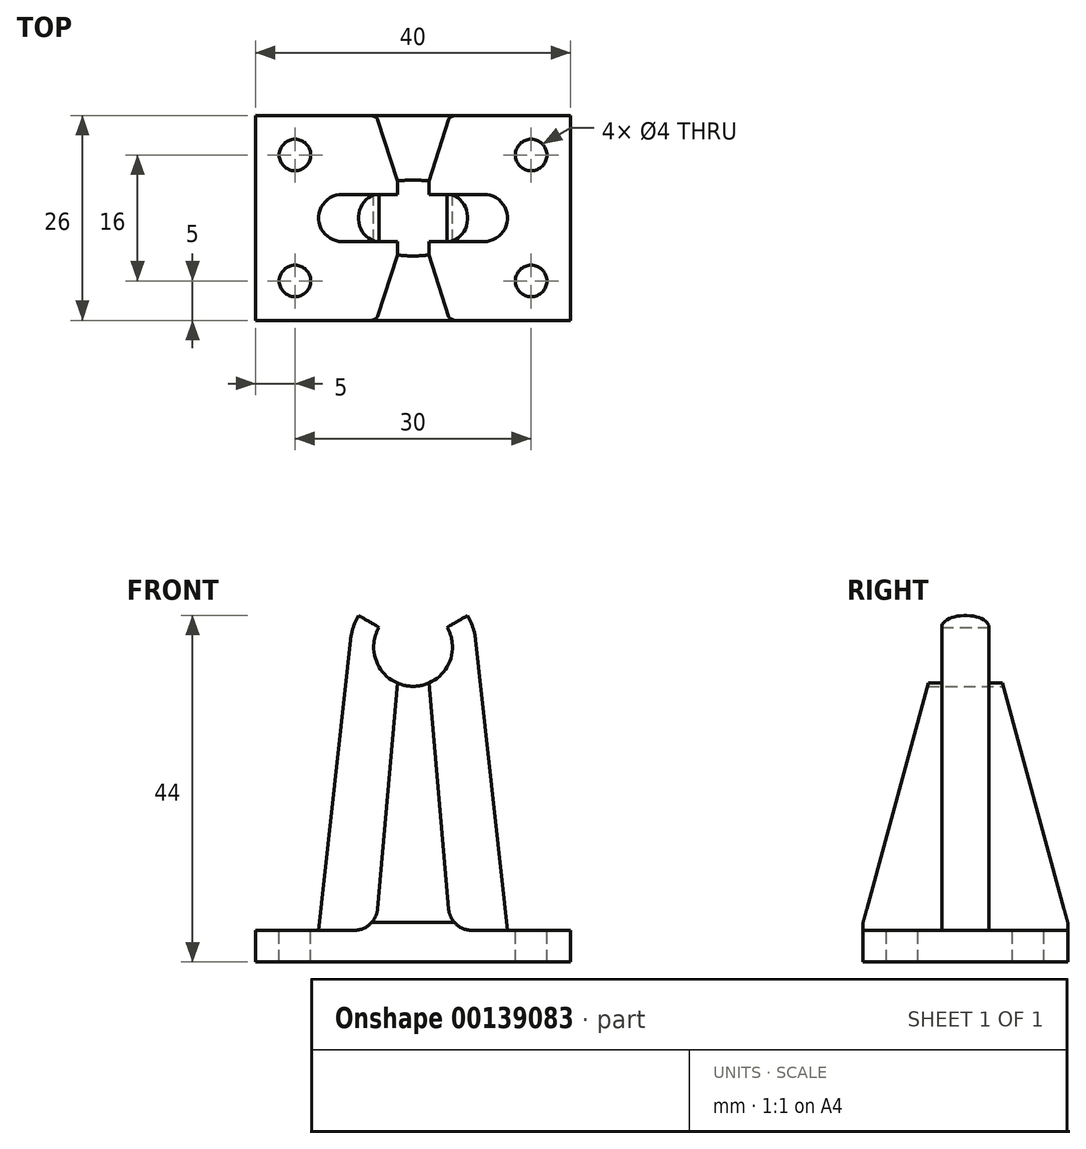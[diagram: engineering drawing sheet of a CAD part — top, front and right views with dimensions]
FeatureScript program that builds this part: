
annotation { "Feature Type Name" : "Feature", "Feature Type Description" : "" }
export const myFeature = defineFeature(function(context is Context, id is Id, definition is map)
    precondition{}
    {
        {
            var Q0;
            Q0=qCreatedBy(makeId("Front.planeOp"),FACE);
            var sketch = newSketch(context, id + "F0", { "sketchPlane" : qUnion([Q0])});
            skLineSegment(sketch, "E0.bottom", {"start": v(0, 0) * mm, "end": v(20, 0) * mm});
            skArc(sketch, "E1", {"start": v(0, 35) * mm, "mid": v(4.33, 37.5) * mm, "end": v(4.33, 42.5) * mm});
            skArc(sketch, "E2", {"start": v(7.95, 40.87) * mm, "mid": v(7.6, 42.49) * mm, "end": v(6.93, 44) * mm});
            skLineSegment(sketch, "E3", {"start": v(0, 0) * mm, "end": v(0, 35) * mm});
            skLineSegment(sketch, "E4", {"start": v(20, 0) * mm, "end": v(20, 4) * mm});
            skLineSegment(sketch, "E5", {"start": v(20, 4) * mm, "end": v(12, 4) * mm});
            skLineSegment(sketch, "E6", {"start": v(12, 4) * mm, "end": v(7.95, 40.87) * mm});
            skLineSegment(sketch, "E7", {"start": v(0, 35) * mm, "end": v(0, 40) * mm, "construction": true});
            skLineSegment(sketch, "E8", {"start": v(0, 40) * mm, "end": v(4.33, 42.5) * mm, "construction": true});
            skLineSegment(sketch, "E9", {"start": v(4.33, 42.5) * mm, "end": v(6.93, 44) * mm});
            skSolve(sketch);
        }
        {
            var Q0;
            Q0=makeQuery(id+"F0.imprint","IMPRINT",FACE,{"disambiguationData":[TD([[makeQuery(id+"F0.imprint","IMPRINT",EDGE,{"derivedFrom":sQuery(id+"F0.wireOp",EDGE,"E0.bottom")}),1.0]])]});
            extrude(context, id + "F1", {"entities" : qUnion([Q0]), "depth" : 3 * mm});
        }
        {
            var Q0;
            Q0=makeQuery(id+"F1.opExtrude","CAP_FACE",FACE,{"disambiguationData":[OSD([sQuery(id+"F0.wireOp",EDGE,"E0.bottom"),sQuery(id+"F0.wireOp",EDGE,"E1"),sQuery(id+"F0.wireOp",EDGE,"E2"),sQuery(id+"F0.wireOp",EDGE,"E3"),sQuery(id+"F0.wireOp",EDGE,"E4"),sQuery(id+"F0.wireOp",EDGE,"E5"),sQuery(id+"F0.wireOp",EDGE,"E6"),sQuery(id+"F0.wireOp",EDGE,"E9")])],"isStart":false});
            var sketch = newSketch(context, id + "F2", { "sketchPlane" : qUnion([Q0])});
            skLineSegment(sketch, "E10.bottom", {"start": v(0, 0) * mm, "end": v(20, 0) * mm});
            skLineSegment(sketch, "E10.right", {"start": v(20, 0) * mm, "end": v(20, 4) * mm});
            skLineSegment(sketch, "E11", {"start": v(20, 4) * mm, "end": v(4.75, 4) * mm});
            skLineSegment(sketch, "E12", {"start": v(0, 0) * mm, "end": v(0, 35) * mm});
            skArc(sketch, "E13.0", {"start": v(0, 35) * mm, "mid": v(1.02, 35.1) * mm, "end": v(2, 35.42) * mm});
            skLineSegment(sketch, "E14", {"start": v(4.75, 4) * mm, "end": v(2, 35.42) * mm});
            skPoint(sketch, "E15.orphan", {"position": v(4.33, 42.5) * mm});
            skSolve(sketch);
        }
        {
            var Q0;
            Q0 = qSketchRegion(id + "F2", true);
            extrude(context, id + "F3", {"entities" : qUnion([Q0]), "operationType" : NewBodyOperationType.ADD, "depth" : 10 * mm});
        }
        {
            var Q0;
            Q0=makeQuery(id+"F3.boolean.opBoolean","MERGE",FACE,{"derivedFrom":[makeQuery(id+"F1.opExtrude","SWEPT_FACE",FACE,{"disambiguationData":[OSD([sQuery(id+"F0.wireOp",EDGE,"E3")])]}),makeQuery(id+"F3.opExtrude","SWEPT_FACE",FACE,{"disambiguationData":[OSD([sQuery(id+"F2.wireOp",EDGE,"E12")])]})]});
            var sketch = newSketch(context, id + "F4", { "sketchPlane" : qUnion([Q0])});
            skLineSegment(sketch, "E16", {"start": v(13, 5) * mm, "end": v(13, 38) * mm});
            skLineSegment(sketch, "E17", {"start": v(13, 38) * mm, "end": v(4, 38) * mm});
            skLineSegment(sketch, "E18", {"start": v(4, 38) * mm, "end": v(13, 5) * mm});
            skSolve(sketch);
        }
        {
            var Q0;
            Q0 = qSketchRegion(id + "F4", true);
            extrude(context, id + "F5", {"entities" : qUnion([Q0]), "operationType" : NewBodyOperationType.REMOVE, "endBound" : BoundingType.THROUGH_ALL, "oppositeDirection" : true, "depth" : 25 * mm});
        }
        {
            var Q0;
            Q0=makeQuery(id+"F3.boolean.opBoolean","MERGE",FACE,{"derivedFrom":[makeQuery(id+"F1.opExtrude","SWEPT_FACE",FACE,{"disambiguationData":[OSD([sQuery(id+"F0.wireOp",EDGE,"E5")])]}),makeQuery(id+"F3.opExtrude","SWEPT_FACE",FACE,{"disambiguationData":[OSD([sQuery(id+"F2.wireOp",EDGE,"E11")])]})]});
            var sketch = newSketch(context, id + "F6", { "sketchPlane" : qUnion([Q0])});
            skCircle(sketch, "E19", {"center": v(15, -8) * mm, "radius": 2 * mm});
            skSolve(sketch);
        }
        {
            var Q0;
            Q0=makeQuery(id+"F6.imprint","IMPRINT",FACE,{"disambiguationData":[TD([[makeQuery(id+"F6.imprint","IMPRINT",EDGE,{"derivedFrom":sQuery(id+"F6.wireOp",EDGE,"E19")}),1.0]])]});
            extrude(context, id + "F7", {"entities" : qUnion([Q0]), "operationType" : NewBodyOperationType.REMOVE, "endBound" : BoundingType.THROUGH_ALL, "oppositeDirection" : true, "depth" : 25 * mm});
        }
        {
            var Q0;
            Q0=makeQuery(id+"F3.opExtrude","CAP_EDGE",EDGE,{"disambiguationData":[OSD([sQuery(id+"F2.wireOp",EDGE,"E14")])],"isStart":true});
            var Q1;
            Q1=makeQuery(id+"F3.opExtrude","CAP_EDGE",EDGE,{"disambiguationData":[OSD([sQuery(id+"F2.wireOp",EDGE,"E11")])],"isStart":true});
            var Q2;
            Q2=makeQuery(id+"F3.opExtrude","SWEPT_EDGE",EDGE,{"disambiguationData":[OSD([sQuery(id+"F2.wireOp",EDGE,"E11"),sQuery(id+"F2.wireOp",EDGE,"E14")])]});
            var Q3;
            Q3=makeQuery(id+"F1.opExtrude","CAP_EDGE",EDGE,{"disambiguationData":[OSD([sQuery(id+"F0.wireOp",EDGE,"E6")])],"isStart":false});
            fillet(context, id + "F8", {"entities" : qUnion([Q0, Q1, Q2, Q3]), "radius" : 3 * mm, "tangentPropagation" : true, "allowEdgeOverflow" : false});
        }
        {
            var Q0;
            Q0=makeQuery(id+"F1.opExtrude","SWEPT_BODY",BODY,{"disambiguationData":[OSD([sQuery(id+"F0.wireOp",EDGE,"E0.bottom"),sQuery(id+"F0.wireOp",EDGE,"E1"),sQuery(id+"F0.wireOp",EDGE,"E2"),sQuery(id+"F0.wireOp",EDGE,"E3"),sQuery(id+"F0.wireOp",EDGE,"E4"),sQuery(id+"F0.wireOp",EDGE,"E5"),sQuery(id+"F0.wireOp",EDGE,"E6"),sQuery(id+"F0.wireOp",EDGE,"E9")])]});
            var Q1;
            Q1=makeQuery(id+"F1.opExtrude","CAP_FACE",FACE,{"disambiguationData":[OSD([sQuery(id+"F0.wireOp",EDGE,"E0.bottom"),sQuery(id+"F0.wireOp",EDGE,"E1"),sQuery(id+"F0.wireOp",EDGE,"E2"),sQuery(id+"F0.wireOp",EDGE,"E3"),sQuery(id+"F0.wireOp",EDGE,"E4"),sQuery(id+"F0.wireOp",EDGE,"E5"),sQuery(id+"F0.wireOp",EDGE,"E6"),sQuery(id+"F0.wireOp",EDGE,"E9")])],"isStart":true});
            mirror(context, id + "F9", {"operationType" : NewBodyOperationType.ADD, "entities" : qUnion([Q0]), "mirrorPlane" : qUnion([Q1])});
        }
        {
            var Q0;
            Q0=makeQuery(id+"F1.opExtrude","SWEPT_BODY",BODY,{"disambiguationData":[OSD([sQuery(id+"F0.wireOp",EDGE,"E0.bottom"),sQuery(id+"F0.wireOp",EDGE,"E1"),sQuery(id+"F0.wireOp",EDGE,"E2"),sQuery(id+"F0.wireOp",EDGE,"E3"),sQuery(id+"F0.wireOp",EDGE,"E4"),sQuery(id+"F0.wireOp",EDGE,"E5"),sQuery(id+"F0.wireOp",EDGE,"E6"),sQuery(id+"F0.wireOp",EDGE,"E9")])]});
            var Q1;
            {var subQ0=makeQuery(id+"F3.boolean.opBoolean","MERGE",FACE,{"derivedFrom":[makeQuery(id+"F1.opExtrude","SWEPT_FACE",FACE,{"disambiguationData":[OSD([sQuery(id+"F0.wireOp",EDGE,"E3")])]}),makeQuery(id+"F3.opExtrude","SWEPT_FACE",FACE,{"disambiguationData":[OSD([sQuery(id+"F2.wireOp",EDGE,"E12")])]})]});Q1=makeQuery(id+"F9.boolean.opBoolean","MERGE",FACE,{"derivedFrom":[subQ0,makeQuery(id+"F9.opPattern","COPY",FACE,{"derivedFrom":subQ0,"instanceName":"1"})]});}
            mirror(context, id + "F10", {"operationType" : NewBodyOperationType.ADD, "entities" : qUnion([Q0]), "mirrorPlane" : qUnion([Q1])});
        }
    });
